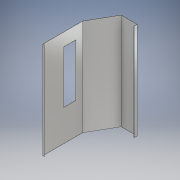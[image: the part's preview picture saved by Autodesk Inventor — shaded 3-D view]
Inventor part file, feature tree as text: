
AUTODESK INVENTOR PART (.ipt)
format: ipt  version: 2018 (Build 220112000, 112)  size: 134,144 bytes
history: native  units: mm
features: extrude x2, sketch x2, plane x1
ambient origin geometry x8: Origin, YZ Plane, XZ Plane, XY Plane, X Axis, Y Axis, Z Axis, Center Point
bodies: Solid1 (feature_tree)
feature tree (5):
  extrude  "main"  Depth=1200.0mm TaperAngle=0.0deg
  plane  "Work Plane1"
  extrude  "Extrusion4"  [1 undecoded]
  sketch  "Sketch1"  dims[d0=150.0deg d7=1200.0mm d8=0.0mm]
  sketch  "Sketch6"  dims[d25=25.5mm d26=0.0mm]
note: 1 required parameter value undecoded (feature->parameter linkage not recoverable at this tier; creation-order binding heuristic only, values carry confidence <= 0.55)
